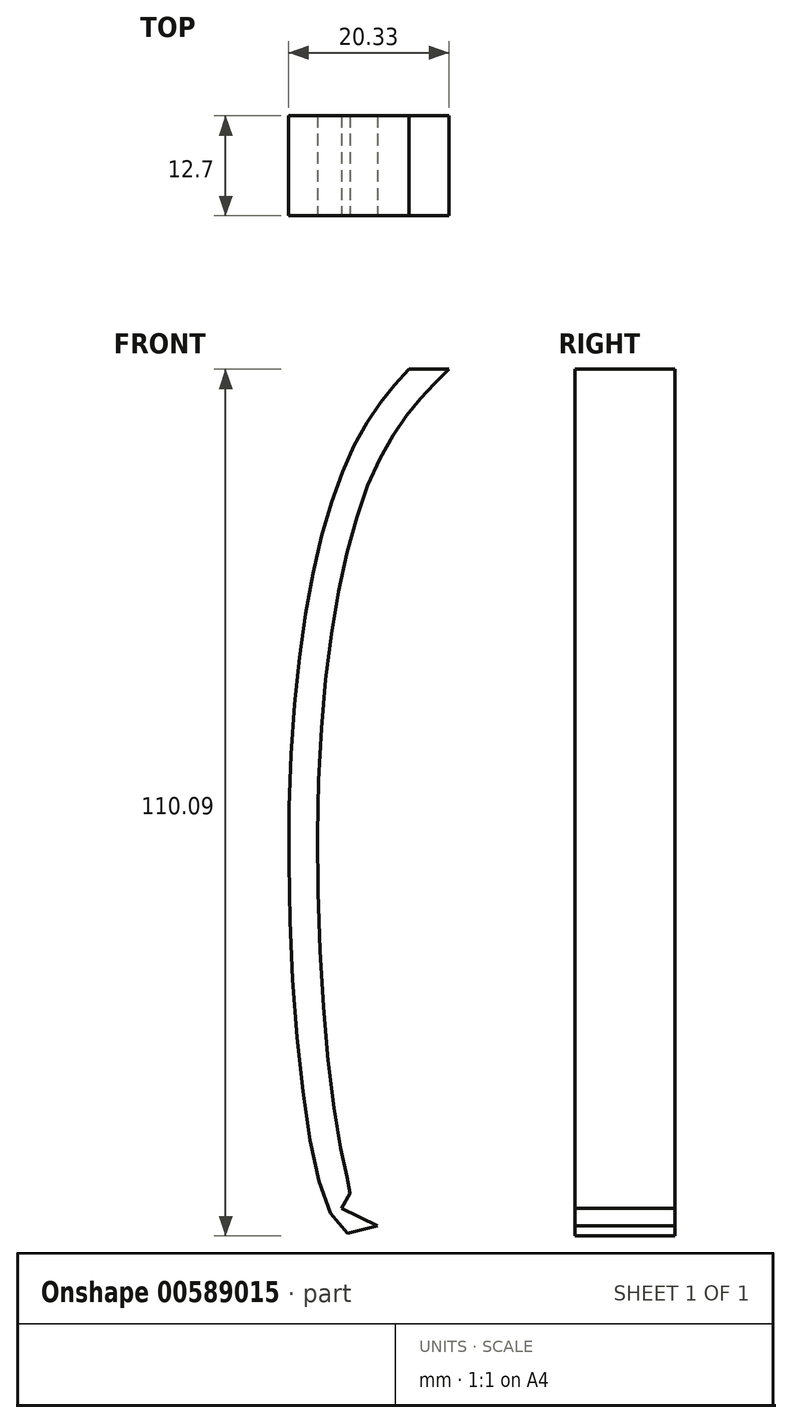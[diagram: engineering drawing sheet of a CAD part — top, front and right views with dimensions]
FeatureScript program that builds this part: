
annotation { "Feature Type Name" : "Feature", "Feature Type Description" : "" }
export const myFeature = defineFeature(function(context is Context, id is Id, definition is map)
    precondition{}
    {
        {
            var Q0;
            Q0=qCreatedBy(makeId("Top.planeOp"),FACE);
            var sketch = newSketch(context, id + "F0", { "sketchPlane" : qUnion([Q0])});
            skLineSegment(sketch, "E0.bottom", {"start": v(-2.54, 12.7) * mm, "end": v(2.54, 12.7) * mm});
            skLineSegment(sketch, "E0.top", {"start": v(-2.54, 0) * mm, "end": v(2.54, 0) * mm});
            skLineSegment(sketch, "E0.left", {"start": v(-2.54, 12.7) * mm, "end": v(-2.54, 0) * mm});
            skLineSegment(sketch, "E0.right", {"start": v(2.54, 12.7) * mm, "end": v(2.54, 0) * mm});
            skSolve(sketch);
        }
        {
            var Q0;
            Q0=qCreatedBy(makeId("Front.planeOp"),FACE);
            var sketch = newSketch(context, id + "F1", { "sketchPlane" : qUnion([Q0])});
            skFitSpline(sketch, "E1", {"points": [v(0, 0) * mm, v(-8.62, -12.26) * mm, v(-15.96, -63.02) * mm, v(-8.78, -107.72) * mm], "startDerivative": vector(-41.04, -41.98) * mm, "endDerivative": vector(33.05, 11.6) * mm});
            skSolve(sketch);
        }
        {
            var Q0;
            Q0=makeQuery(id+"F0.imprint","IMPRINT",FACE,{"disambiguationData":[TD([[makeQuery(id+"F0.imprint","IMPRINT",EDGE,{"derivedFrom":sQuery(id+"F0.wireOp",EDGE,"E0.bottom")}),-1.0]])]});
            var Q1;
            Q1=sQuery(id+"F1.wireOp",EDGE,"E1");
            var Q2;
            Q2=sQuery(id+"F1.wireOp",EDGE,"057f04be-de60-4269-a08e-9da269efc2c5");
            sweep(context, id + "F2", {"profiles" : qUnion([Q0]), "path" : qUnion([Q1, Q2])});
        }
        {
            var Q0;
            Q0=qCreatedBy(makeId("Front.planeOp"),FACE);
            var sketch = newSketch(context, id + "F3", { "sketchPlane" : qUnion([Q0])});
            skCircle(sketch, "E2", {"center": v(0, 0) * mm, "radius": 9.53 * mm});
            skSolve(sketch);
        }
        {
            var Q0;
            Q0=sQuery(id+"F3.wireOp",EDGE,"E2");
            extrude(context, id + "F4", {"bodyType" : ToolBodyType.SURFACE, "operationType" : NewBodyOperationType.ADD, "surfaceEntities" : qUnion([Q0]), "oppositeDirection" : true, "depth" : 25.4 * mm, "offsetDistance" : 25.4 * mm});
        }
        {
            var Q0;
            Q0=makeQuery(id+"F4.opExtrude","SWEPT_BODY",BODY,{"disambiguationData":[OSD([sQuery(id+"F3.wireOp",EDGE,"E2")])]});
            var Q1;
            Q1=makeQuery(id+"F2.opSweep","CAP_EDGE",EDGE,{"disambiguationData":[OSD([sQuery(id+"F0.wireOp",EDGE,"E0.top"),sQuery(id+"F1.wireOp",VERTEX,"E1.start")])],"isStart":true});
            transform(context, id + "F5", {"entities" : qUnion([Q0]), "transformType" : TransformType.ROTATION, "transformAxis" : qUnion([Q1]), "angle" : 90 * degree, "oppositeDirection" : true, "makeCopy" : false});
        }
        {
            var Q0;
            Q0=makeQuery(id+"F4.opExtrude","SWEPT_BODY",BODY,{"disambiguationData":[OSD([sQuery(id+"F3.wireOp",EDGE,"E2")])]});
            transform(context, id + "F6", {"entities" : qUnion([Q0]), "transformType" : TransformType.TRANSLATION_3D, "dx" : 5.6 * mm, "dy" : 4.83 * mm, "dz" : 0 * mm, "makeCopy" : false});
        }
    });
